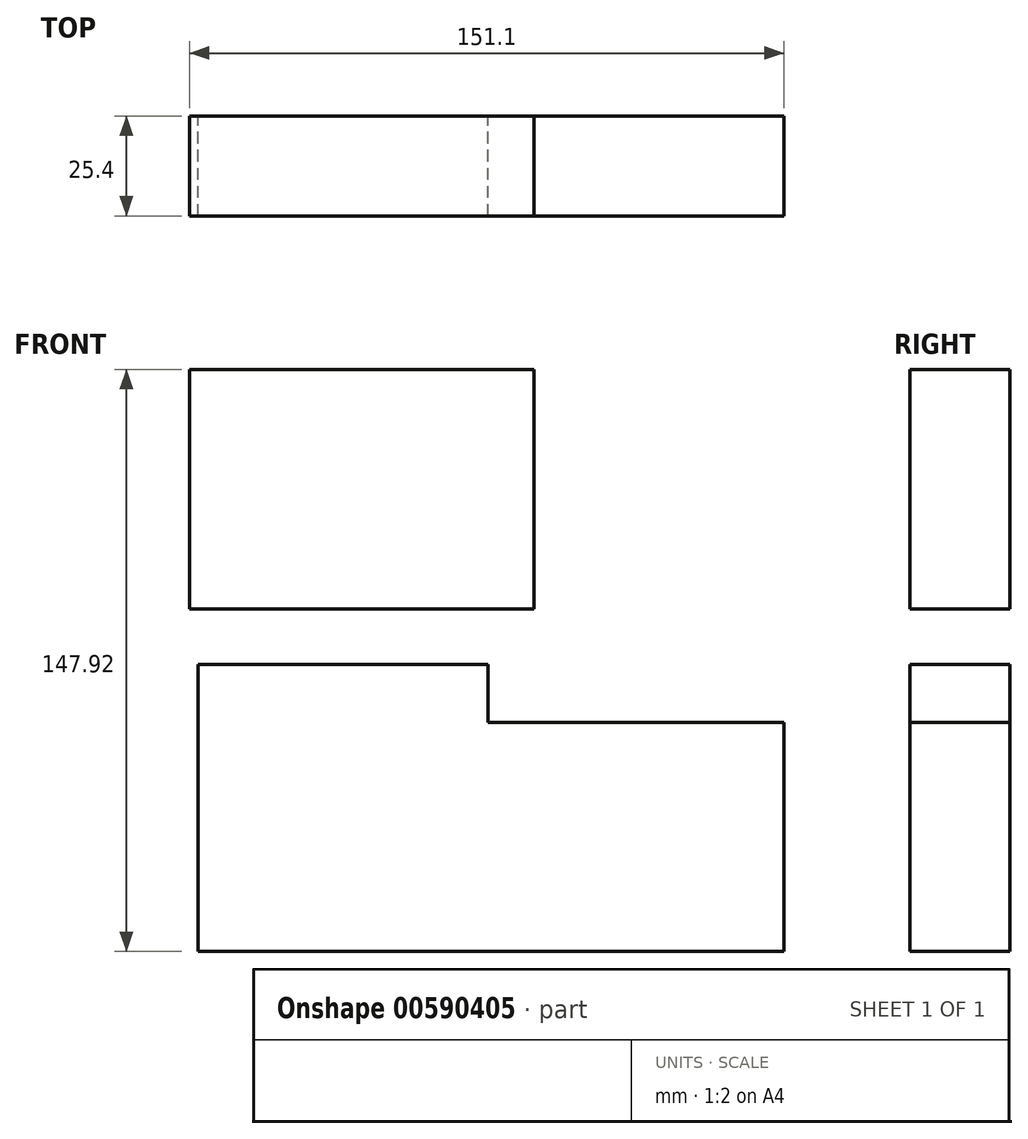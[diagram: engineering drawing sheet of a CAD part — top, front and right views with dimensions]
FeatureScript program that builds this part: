
annotation { "Feature Type Name" : "Feature", "Feature Type Description" : "" }
export const myFeature = defineFeature(function(context is Context, id is Id, definition is map)
    precondition{}
    {
        {
            var Q0;
            Q0=qCreatedBy(makeId("Front.planeOp"),FACE);
            var sketch = newSketch(context, id + "F0", { "sketchPlane" : qUnion([Q0])});
            skLineSegment(sketch, "E0.bottom", {"start": v(-75.8, 74.94) * mm, "end": v(11.79, 74.94) * mm});
            skLineSegment(sketch, "E0.top", {"start": v(-75.8, 14.03) * mm, "end": v(11.79, 14.03) * mm});
            skLineSegment(sketch, "E0.left", {"start": v(-75.8, 74.94) * mm, "end": v(-75.8, 14.03) * mm});
            skLineSegment(sketch, "E0.right", {"start": v(11.79, 74.94) * mm, "end": v(11.79, 14.03) * mm});
            skSolve(sketch);
        }
        {
            var Q0;
            Q0 = qSketchRegion(id + "F0", true);
            extrude(context, id + "F1", {"entities" : qUnion([Q0]), "depth" : 25.4 * mm, "offsetDistance" : 25.4 * mm});
        }
        {
            var Q0;
            Q0=qCreatedBy(makeId("Front.planeOp"),FACE);
            var sketch = newSketch(context, id + "F2", { "sketchPlane" : qUnion([Q0])});
            skLineSegment(sketch, "E1.bottom", {"start": v(-73.6, -72.98) * mm, "end": v(0, -72.98) * mm});
            skLineSegment(sketch, "E1.top", {"start": v(-73.6, 0) * mm, "end": v(0, 0) * mm});
            skLineSegment(sketch, "E1.left", {"start": v(-73.6, -72.98) * mm, "end": v(-73.6, 0) * mm});
            skLineSegment(sketch, "E1.right", {"start": v(0, -72.98) * mm, "end": v(0, 0) * mm});
            skLineSegment(sketch, "E2.bottom", {"start": v(0, -72.98) * mm, "end": v(75.29, -72.98) * mm});
            skLineSegment(sketch, "E2.top", {"start": v(0, -14.8) * mm, "end": v(75.29, -14.8) * mm});
            skLineSegment(sketch, "E2.left", {"start": v(0, -72.98) * mm, "end": v(0, -14.8) * mm});
            skLineSegment(sketch, "E2.right", {"start": v(75.29, -72.98) * mm, "end": v(75.29, -14.8) * mm});
            skSolve(sketch);
        }
        {
            var Q0;
            Q0 = qSketchRegion(id + "F2", true);
            extrude(context, id + "F3", {"entities" : qUnion([Q0]), "depth" : 25.4 * mm, "offsetDistance" : 25.4 * mm});
        }
    });
